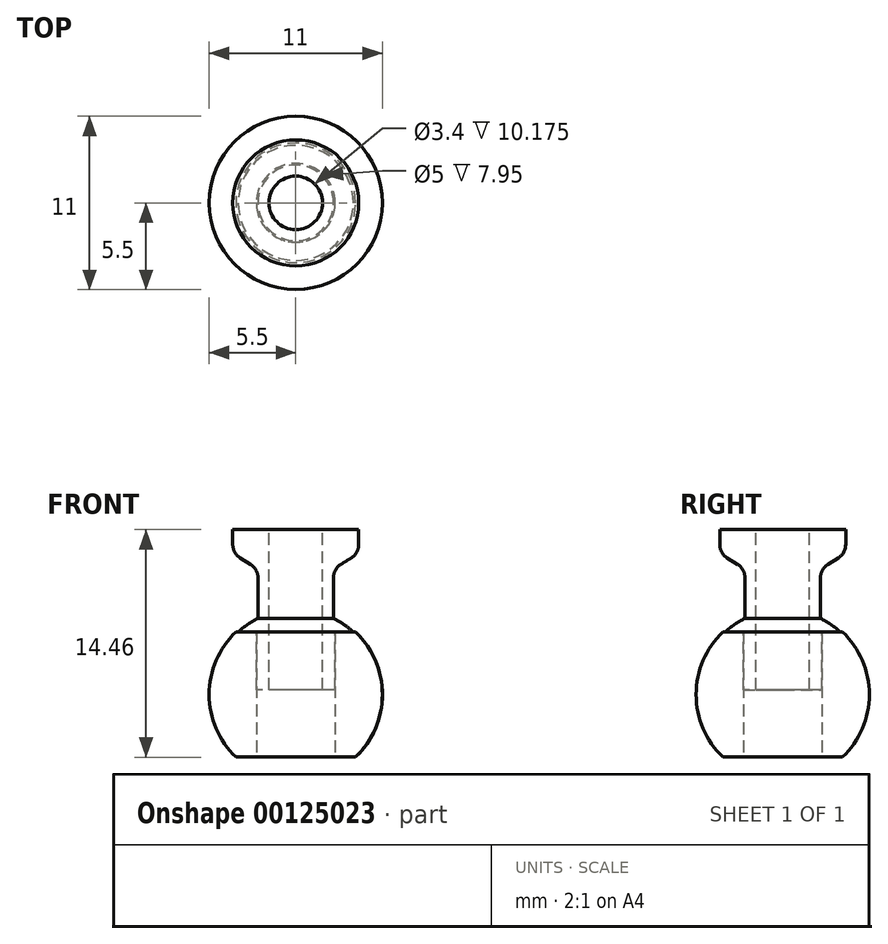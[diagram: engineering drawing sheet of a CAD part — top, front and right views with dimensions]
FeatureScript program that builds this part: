
annotation { "Feature Type Name" : "Feature", "Feature Type Description" : "" }
export const myFeature = defineFeature(function(context is Context, id is Id, definition is map)
    precondition{}
    {
        {
            var Q0;
            Q0=qCreatedBy(makeId("Front.planeOp"),FACE);
            var sketch = newSketch(context, id + "F0", { "sketchPlane" : qUnion([Q0])});
            skArc(sketch, "E0", {"start": v(-3.8, 3.97) * mm, "mid": v(-5.5, 0) * mm, "end": v(-3.8, -3.98) * mm});
            skLineSegment(sketch, "E1", {"start": v(0, 3.98) * mm, "end": v(0, -3.98) * mm});
            skLineSegment(sketch, "E2", {"start": v(0, 3.98) * mm, "end": v(-3.8, 3.98) * mm});
            skLineSegment(sketch, "E3", {"start": v(0, -3.98) * mm, "end": v(-3.8, -3.98) * mm});
            skSolve(sketch);
        }
        {
            var Q0;
            Q0=qSketchRegion(id+"F0",true);
            var Q1;
            Q1=sQuery(id+"F0.wireOp",EDGE,"E1");
            revolve(context, id + "F1", {"entities" : qUnion([Q0]), "axis" : qUnion([Q1]), "revolveType" : RevolveType.FULL});
        }
        {
            var Q0;
            Q0=makeQuery(id+"F1.opRevolve","SWEPT_FACE",FACE,{"disambiguationData":[OSD([sQuery(id+"F0.wireOp",EDGE,"E3")])]});
            var sketch = newSketch(context, id + "F2", { "sketchPlane" : qUnion([Q0])});
            skCircle(sketch, "E4", {"center": v(0, 0) * mm, "radius": 2.5 * mm});
            skSolve(sketch);
        }
        {
            var Q0;
            Q0=makeQuery(id+"F2.imprint","IMPRINT",FACE,{"disambiguationData":[TD([[makeQuery(id+"F2.imprint","IMPRINT",EDGE,{"derivedFrom":sQuery(id+"F2.wireOp",EDGE,"E4")}),1.0]])]});
            var Q1;
            Q1=makeQuery(id+"F1.opRevolve","SWEPT_FACE",FACE,{"disambiguationData":[OSD([sQuery(id+"F0.wireOp",EDGE,"E2")])]});
            extrude(context, id + "F3", {"entities" : qUnion([Q0]), "operationType" : NewBodyOperationType.REMOVE, "endBound" : BoundingType.UP_TO_SURFACE, "oppositeDirection" : true, "endBoundEntityFace" : qUnion([Q1]), "depth" : 25 * mm});
        }
        {
            var Q0;
            Q0=qCreatedBy(makeId("Front.planeOp"),FACE);
            var sketch = newSketch(context, id + "F4", { "sketchPlane" : qUnion([Q0])});
            skLineSegment(sketch, "E5", {"start": v(0, 10.47) * mm, "end": v(0, 0.3) * mm});
            skLineSegment(sketch, "E6", {"start": v(0, 0.3) * mm, "end": v(-2.5, 0.3) * mm});
            skLineSegment(sketch, "E7", {"start": v(-2.5, 0.3) * mm, "end": v(-2.5, 3.98) * mm});
            skLineSegment(sketch, "E8", {"start": v(-2.5, 3.98) * mm, "end": v(-3.66, 3.98) * mm});
            skCircle(sketch, "E9", {"center": v(0, 0) * mm, "radius": 5.4 * mm, "construction": true});
            skLineSegment(sketch, "E10", {"start": v(0, 10.47) * mm, "end": v(-4, 10.47) * mm});
            skLineSegment(sketch, "E11", {"start": v(-4, 10.47) * mm, "end": v(-4, 8.97) * mm});
            skLineSegment(sketch, "E12", {"start": v(-4, 8.97) * mm, "end": v(-2.4, 7.97) * mm});
            skLineSegment(sketch, "E13", {"start": v(-2.4, 7.97) * mm, "end": v(-2.4, 4.84) * mm});
            skArc(sketch, "E14", {"start": v(-2.4, 4.84) * mm, "mid": v(-3.06, 4.45) * mm, "end": v(-3.66, 3.98) * mm});
            skSolve(sketch);
        }
        {
            var Q0;
            Q0=makeQuery(id+"F4.imprint","IMPRINT",FACE,{"disambiguationData":[TD([[makeQuery(id+"F4.imprint","IMPRINT",EDGE,{"derivedFrom":sQuery(id+"F4.wireOp",EDGE,"E5")}),-1.0]])]});
            var Q1;
            Q1=sQuery(id+"F4.wireOp",EDGE,"E5");
            revolve(context, id + "F5", {"entities" : qUnion([Q0]), "axis" : qUnion([Q1]), "revolveType" : RevolveType.FULL});
        }
        {
            var Q0;
            Q0=makeQuery(id+"F5.opRevolve","SWEPT_FACE",FACE,{"disambiguationData":[OSD([sQuery(id+"F4.wireOp",EDGE,"E10")])]});
            var sketch = newSketch(context, id + "F6", { "sketchPlane" : qUnion([Q0])});
            skCircle(sketch, "E15", {"center": v(0, 0) * mm, "radius": 1.7 * mm});
            skSolve(sketch);
        }
        {
            var Q0;
            Q0=makeQuery(id+"F6.imprint","IMPRINT",FACE,{"disambiguationData":[TD([[makeQuery(id+"F6.imprint","IMPRINT",EDGE,{"derivedFrom":sQuery(id+"F6.wireOp",EDGE,"E15")}),1.0]])]});
            var Q1;
            Q1=makeQuery(id+"F5.opRevolve","SWEPT_FACE",FACE,{"disambiguationData":[OSD([sQuery(id+"F4.wireOp",EDGE,"E6")])]});
            extrude(context, id + "F7", {"entities" : qUnion([Q0]), "operationType" : NewBodyOperationType.REMOVE, "endBound" : BoundingType.UP_TO_SURFACE, "oppositeDirection" : true, "endBoundEntityFace" : qUnion([Q1]), "depth" : 25 * mm});
        }
        {
            var Q0;
            Q0=makeQuery(id+"F5.opRevolve","SWEPT_EDGE",EDGE,{"disambiguationData":[OSD([sQuery(id+"F4.wireOp",EDGE,"E12"),sQuery(id+"F4.wireOp",EDGE,"E13")])]});
            fillet(context, id + "F8", {"entities" : qUnion([Q0]), "radius" : 1 * mm, "tangentPropagation" : true, "allowEdgeOverflow" : false});
        }
        {
            var Q0;
            Q0=makeQuery(id+"F5.opRevolve","SWEPT_EDGE",EDGE,{"disambiguationData":[OSD([sQuery(id+"F4.wireOp",EDGE,"E11"),sQuery(id+"F4.wireOp",EDGE,"E12")])]});
            fillet(context, id + "F9", {"entities" : qUnion([Q0]), "radius" : 1 * mm, "tangentPropagation" : true, "allowEdgeOverflow" : false});
        }
    });
